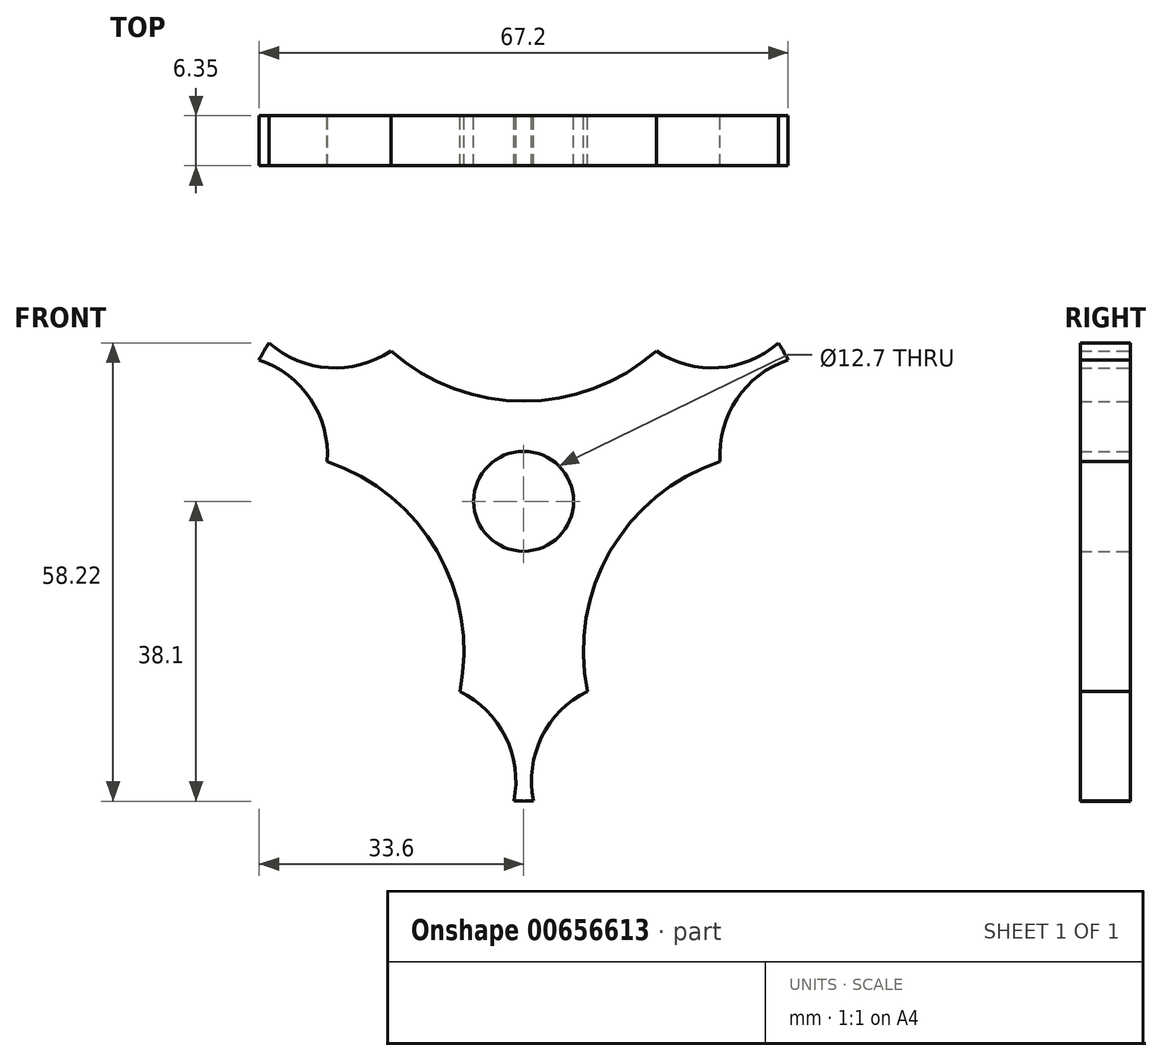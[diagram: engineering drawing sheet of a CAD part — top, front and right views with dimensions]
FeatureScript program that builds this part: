
annotation { "Feature Type Name" : "Feature", "Feature Type Description" : "" }
export const myFeature = defineFeature(function(context is Context, id is Id, definition is map)
    precondition{}
    {
        {
            var Q0;
            Q0=qCreatedBy(makeId("Front.planeOp"),FACE);
            var sketch = newSketch(context, id + "F0", { "sketchPlane" : qUnion([Q0])});
            skCircle(sketch, "E0", {"center": v(0, 0) * mm, "radius": 38.1 * mm});
            skCircle(sketch, "E1", {"center": v(0, 0) * mm, "radius": 6.35 * mm});
            skCircle(sketch, "E2", {"center": v(0, 38.1) * mm, "radius": 25.4 * mm});
            skCircle(sketch, "E3.1.0", {"center": v(-33, -19.05) * mm, "radius": 25.4 * mm});
            skCircle(sketch, "E3.2.0", {"center": v(33, -19.05) * mm, "radius": 25.4 * mm});
            skCircle(sketch, "E4", {"center": v(-23.95, 29.63) * mm, "radius": 12.7 * mm});
            skCircle(sketch, "E5", {"center": v(23.95, 29.63) * mm, "radius": 12.7 * mm});
            skCircle(sketch, "E6", {"center": v(37.64, 5.92) * mm, "radius": 12.7 * mm});
            skCircle(sketch, "E7", {"center": v(13.69, -35.56) * mm, "radius": 12.7 * mm});
            skCircle(sketch, "E8", {"center": v(-13.69, -35.56) * mm, "radius": 12.7 * mm});
            skCircle(sketch, "E9", {"center": v(-37.64, 5.92) * mm, "radius": 12.7 * mm});
            skSolve(sketch);
        }
        {
            var Q0;
            Q0=makeQuery(id+"F0.imprint","IMPRINT",FACE,{"disambiguationData":[TD([[makeQuery(id+"F0.imprint","IMPRINT",EDGE,{"derivedFrom":sQuery(id+"F0.wireOp",EDGE,"E1")}),-1.0]])]});
            extrude(context, id + "F1", {"entities" : qUnion([Q0]), "depth" : 6.35 * mm, "offsetDistance" : 25.4 * mm});
        }
    });
